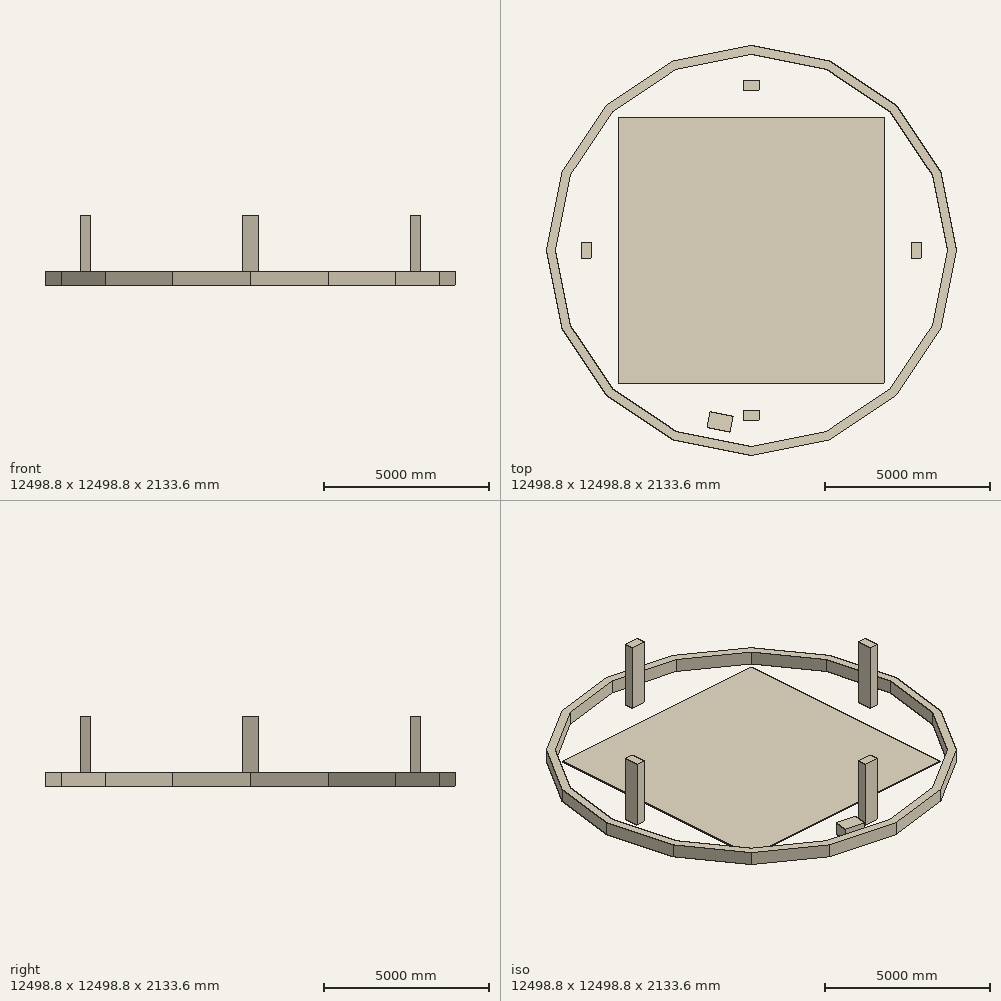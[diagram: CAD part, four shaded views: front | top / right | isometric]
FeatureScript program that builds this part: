
annotation { "Feature Type Name" : "Feature", "Feature Type Description" : "" }
export const myFeature = defineFeature(function(context is Context, id is Id, definition is map)
    precondition{}
    {
        {
            var Q0;
            Q0=qCreatedBy(makeId("Top.planeOp"),FACE);
            var sketch = newSketch(context, id + "F0", { "sketchPlane" : qUnion([Q0])});
            skCircle(sketch, "E0.cCircle", {"center": v(0, 0) * mm, "radius": 6129.33 * mm, "construction": true});
            skLineSegment(sketch, "E0.0", {"start": v(4419, -4419) * mm, "end": v(2391.55, -5773.7) * mm});
            skLineSegment(sketch, "E0.1", {"start": v(2391.55, -5773.7) * mm, "end": v(0, -6249.41) * mm});
            skLineSegment(sketch, "E0.2", {"start": v(0, -6249.41) * mm, "end": v(-2391.55, -5773.7) * mm});
            skLineSegment(sketch, "E0.3", {"start": v(-2391.55, -5773.7) * mm, "end": v(-4419, -4419) * mm});
            skLineSegment(sketch, "E0.4", {"start": v(-4419, -4419) * mm, "end": v(-5773.7, -2391.55) * mm});
            skLineSegment(sketch, "E0.5", {"start": v(-5773.7, -2391.55) * mm, "end": v(-6249.41, 0) * mm});
            skLineSegment(sketch, "E0.6", {"start": v(-6249.41, 0) * mm, "end": v(-5773.7, 2391.55) * mm});
            skLineSegment(sketch, "E0.7", {"start": v(-5773.7, 2391.55) * mm, "end": v(-4419, 4419) * mm});
            skLineSegment(sketch, "E0.8", {"start": v(-4419, 4419) * mm, "end": v(-2391.55, 5773.7) * mm});
            skLineSegment(sketch, "E0.9", {"start": v(-2391.55, 5773.7) * mm, "end": v(0, 6249.41) * mm});
            skLineSegment(sketch, "E0.10", {"start": v(0, 6249.41) * mm, "end": v(2391.55, 5773.7) * mm});
            skLineSegment(sketch, "E0.11", {"start": v(2391.55, 5773.7) * mm, "end": v(4419, 4419) * mm});
            skLineSegment(sketch, "E0.12", {"start": v(4419, 4419) * mm, "end": v(5773.7, 2391.55) * mm});
            skLineSegment(sketch, "E0.13", {"start": v(5773.7, 2391.55) * mm, "end": v(6249.41, 0) * mm});
            skLineSegment(sketch, "E0.14", {"start": v(6249.41, 0) * mm, "end": v(5773.7, -2391.55) * mm});
            skLineSegment(sketch, "E0.15", {"start": v(5773.7, -2391.55) * mm, "end": v(4419, -4419) * mm});
            skPoint(sketch, "E0.0.midPoint", {"position": v(3405.27, -5096.35) * mm});
            skCircle(sketch, "E1.cCircle", {"center": v(0, 0) * mm, "radius": 5862.63 * mm, "construction": true});
            skLineSegment(sketch, "E1.0", {"start": v(4226.72, 4226.72) * mm, "end": v(5522.48, 2287.49) * mm});
            skLineSegment(sketch, "E1.1", {"start": v(5522.48, 2287.49) * mm, "end": v(5977.49, 0) * mm});
            skLineSegment(sketch, "E1.2", {"start": v(5977.49, 0) * mm, "end": v(5522.48, -2287.49) * mm});
            skLineSegment(sketch, "E1.3", {"start": v(5522.48, -2287.49) * mm, "end": v(4226.72, -4226.72) * mm});
            skLineSegment(sketch, "E1.4", {"start": v(4226.72, -4226.72) * mm, "end": v(2287.49, -5522.48) * mm});
            skLineSegment(sketch, "E1.5", {"start": v(2287.49, -5522.48) * mm, "end": v(0, -5977.49) * mm});
            skLineSegment(sketch, "E1.6", {"start": v(0, -5977.49) * mm, "end": v(-2287.49, -5522.48) * mm});
            skLineSegment(sketch, "E1.7", {"start": v(-2287.49, -5522.48) * mm, "end": v(-4226.72, -4226.72) * mm});
            skLineSegment(sketch, "E1.8", {"start": v(-4226.72, -4226.72) * mm, "end": v(-5522.48, -2287.49) * mm});
            skLineSegment(sketch, "E1.9", {"start": v(-5522.48, -2287.49) * mm, "end": v(-5977.49, 0) * mm});
            skLineSegment(sketch, "E1.10", {"start": v(-5977.49, 0) * mm, "end": v(-5522.48, 2287.49) * mm});
            skLineSegment(sketch, "E1.11", {"start": v(-5522.48, 2287.49) * mm, "end": v(-4226.72, 4226.72) * mm});
            skLineSegment(sketch, "E1.12", {"start": v(-4226.72, 4226.72) * mm, "end": v(-2287.49, 5522.48) * mm});
            skLineSegment(sketch, "E1.13", {"start": v(-2287.49, 5522.48) * mm, "end": v(0, 5977.49) * mm});
            skLineSegment(sketch, "E1.14", {"start": v(0, 5977.49) * mm, "end": v(2287.49, 5522.48) * mm});
            skLineSegment(sketch, "E1.15", {"start": v(2287.49, 5522.48) * mm, "end": v(4226.72, 4226.72) * mm});
            skPoint(sketch, "E1.0.midPoint", {"position": v(4874.6, 3257.1) * mm});
            skLineSegment(sketch, "E2.bottom", {"start": v(-254, 5181.6) * mm, "end": v(254, 5181.6) * mm});
            skLineSegment(sketch, "E2.top", {"start": v(-254, 4876.8) * mm, "end": v(254, 4876.8) * mm});
            skLineSegment(sketch, "E2.left", {"start": v(-254, 5181.6) * mm, "end": v(-254, 4876.8) * mm});
            skLineSegment(sketch, "E2.right", {"start": v(254, 5181.6) * mm, "end": v(254, 4876.8) * mm});
            skLineSegment(sketch, "E3.bottom", {"start": v(-254, -4876.8) * mm, "end": v(254, -4876.8) * mm});
            skLineSegment(sketch, "E3.top", {"start": v(-254, -5181.6) * mm, "end": v(254, -5181.6) * mm});
            skLineSegment(sketch, "E3.left", {"start": v(-254, -4876.8) * mm, "end": v(-254, -5181.6) * mm});
            skLineSegment(sketch, "E3.right", {"start": v(254, -4876.8) * mm, "end": v(254, -5181.6) * mm});
            skLineSegment(sketch, "E4", {"start": v(-4876.8, 0) * mm, "end": v(0, 0) * mm, "construction": true});
            skLineSegment(sketch, "E5", {"start": v(4876.8, 0) * mm, "end": v(0, 0) * mm, "construction": true});
            skLineSegment(sketch, "E6", {"start": v(0, 4876.8) * mm, "end": v(0, 0) * mm, "construction": true});
            skLineSegment(sketch, "E7", {"start": v(0, -4876.8) * mm, "end": v(0, 0) * mm, "construction": true});
            skLineSegment(sketch, "E8.bottom", {"start": v(4876.8, 254) * mm, "end": v(5181.6, 254) * mm});
            skLineSegment(sketch, "E8.top", {"start": v(4876.8, -254) * mm, "end": v(5181.6, -254) * mm});
            skLineSegment(sketch, "E8.left", {"start": v(4876.8, 254) * mm, "end": v(4876.8, -254) * mm});
            skLineSegment(sketch, "E8.right", {"start": v(5181.6, 254) * mm, "end": v(5181.6, -254) * mm});
            skPoint(sketch, "E9", {"position": v(4876.8, 0) * mm});
            skLineSegment(sketch, "E10.bottom", {"start": v(-5181.6, 254) * mm, "end": v(-4876.8, 254) * mm});
            skLineSegment(sketch, "E10.top", {"start": v(-5181.6, -254) * mm, "end": v(-4876.8, -254) * mm});
            skLineSegment(sketch, "E10.left", {"start": v(-5181.6, 254) * mm, "end": v(-5181.6, -254) * mm});
            skLineSegment(sketch, "E10.right", {"start": v(-4876.8, 254) * mm, "end": v(-4876.8, -254) * mm});
            skPoint(sketch, "E11", {"position": v(-4876.8, 0) * mm});
            skPoint(sketch, "E12", {"position": v(1143.74, 5749.98) * mm});
            skLineSegment(sketch, "E13.bottom", {"start": v(4064, 4064) * mm, "end": v(-4064, 4064) * mm});
            skLineSegment(sketch, "E13.top", {"start": v(4064, -4064) * mm, "end": v(-4064, -4064) * mm});
            skLineSegment(sketch, "E13.left", {"start": v(4064, 4064) * mm, "end": v(4064, -4064) * mm});
            skLineSegment(sketch, "E13.right", {"start": v(-4064, 4064) * mm, "end": v(-4064, -4064) * mm});
            skLineSegment(sketch, "E14.bottom", {"start": v(-1262.56, -4917.05) * mm, "end": v(-558.8, -5057.04) * mm});
            skLineSegment(sketch, "E14.top", {"start": v(-1357.95, -5396.6) * mm, "end": v(-654.19, -5536.6) * mm});
            skLineSegment(sketch, "E14.left", {"start": v(-1262.56, -4917.05) * mm, "end": v(-1357.95, -5396.6) * mm});
            skLineSegment(sketch, "E14.right", {"start": v(-558.8, -5057.04) * mm, "end": v(-654.19, -5536.6) * mm});
            skLineSegment(sketch, "E15", {"start": v(-1357.95, -5396.6) * mm, "end": v(-1417.42, -5695.55) * mm});
            skLineSegment(sketch, "E16", {"start": v(-654.19, -5536.6) * mm, "end": v(-713.65, -5835.53) * mm});
            skSolve(sketch);
        }
        {
            var Q0;
            Q0=makeQuery(id+"F0.imprint","IMPRINT",FACE,{"disambiguationData":[TD([[makeQuery(id+"F0.imprint","IMPRINT",EDGE,{"derivedFrom":sQuery(id+"F0.wireOp",EDGE,"E10.bottom")}),-1.0]])]});
            var Q1;
            Q1=makeQuery(id+"F0.imprint","IMPRINT",FACE,{"disambiguationData":[TD([[makeQuery(id+"F0.imprint","IMPRINT",EDGE,{"derivedFrom":sQuery(id+"F0.wireOp",EDGE,"E2.bottom")}),-1.0]])]});
            var Q2;
            Q2=makeQuery(id+"F0.imprint","IMPRINT",FACE,{"disambiguationData":[TD([[makeQuery(id+"F0.imprint","IMPRINT",EDGE,{"derivedFrom":sQuery(id+"F0.wireOp",EDGE,"E8.bottom")}),-1.0]])]});
            var Q3;
            Q3=makeQuery(id+"F0.imprint","IMPRINT",FACE,{"disambiguationData":[TD([[makeQuery(id+"F0.imprint","IMPRINT",EDGE,{"derivedFrom":sQuery(id+"F0.wireOp",EDGE,"E3.bottom")}),-1.0]])]});
            extrude(context, id + "F1", {"entities" : qUnion([Q0, Q1, Q2, Q3]), "depth" : 2133.6 * mm, "offsetDistance" : 25.4 * mm});
        }
        {
            var Q0;
            Q0 = qSketchRegion(id + "F0", true);
            extrude(context, id + "F2", {"entities" : qUnion([Q0]), "depth" : 419.1 * mm, "offsetDistance" : 25.4 * mm});
        }
        {
            var Q0;
            Q0=makeQuery(id+"F0.imprint","IMPRINT",FACE,{"disambiguationData":[TD([[makeQuery(id+"F0.imprint","IMPRINT",EDGE,{"derivedFrom":sQuery(id+"F0.wireOp",EDGE,"E13.bottom")}),1.0]])]});
            extrude(context, id + "F3", {"entities" : qUnion([Q0]), "depth" : 25.4 * mm, "offsetDistance" : 25.4 * mm});
        }
        {
            var Q0;
            Q0=makeQuery(id+"F0.imprint","IMPRINT",FACE,{"disambiguationData":[TD([[makeQuery(id+"F0.imprint","IMPRINT",EDGE,{"derivedFrom":sQuery(id+"F0.wireOp",EDGE,"E14.bottom")}),-1.0]])]});
            var Q1;
            Q1=sQuery(id+"F0.wireOp",EDGE,"E14.left");
            var Q2;
            Q2=sQuery(id+"F0.wireOp",EDGE,"E14.bottom");
            var Q3;
            Q3=sQuery(id+"F0.wireOp",EDGE,"E14.right");
            var Q4;
            Q4=sQuery(id+"F0.wireOp",EDGE,"E14.top");
            extrude(context, id + "F4", {"entities" : qUnion([Q0]), "surfaceEntities" : qUnion([Q1, Q2, Q3, Q4]), "depth" : 387.35 * mm, "offsetDistance" : 25.4 * mm});
        }
    });
